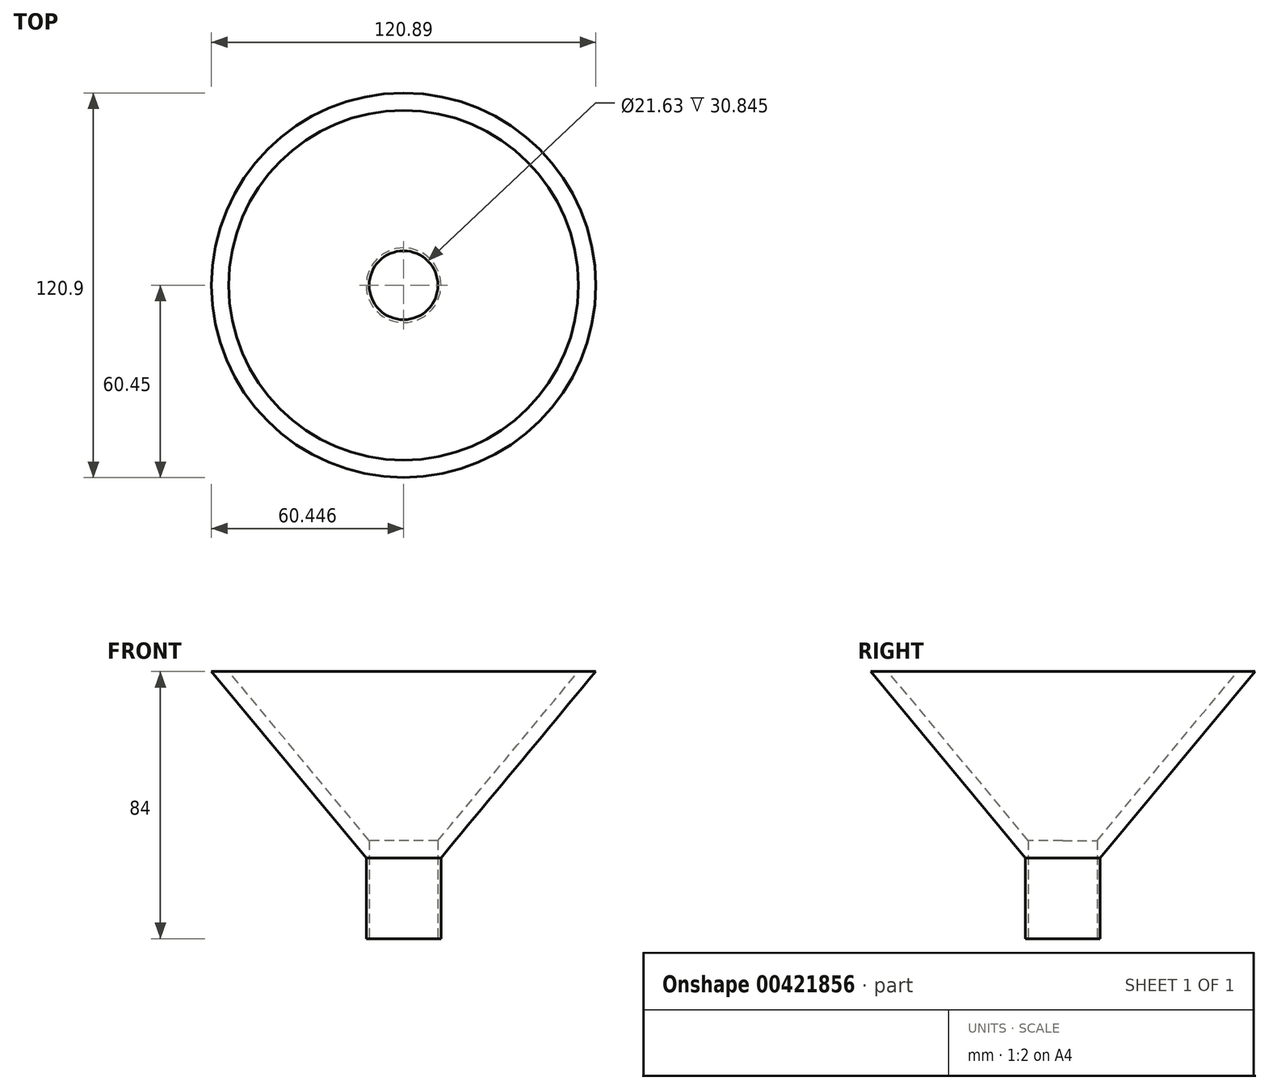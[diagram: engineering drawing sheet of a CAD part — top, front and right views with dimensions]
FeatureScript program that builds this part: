
annotation { "Feature Type Name" : "Feature", "Feature Type Description" : "" }
export const myFeature = defineFeature(function(context is Context, id is Id, definition is map)
    precondition{}
    {
        {
            var Q0;
            Q0=qCreatedBy(makeId("Front.planeOp"),FACE);
            var sketch = newSketch(context, id + "F0", { "sketchPlane" : qUnion([Q0])});
            skLineSegment(sketch, "E0", {"start": v(0, 0) * mm, "end": v(0, -25.4) * mm});
            skLineSegment(sketch, "E1", {"start": v(0, -25.4) * mm, "end": v(0, 0) * mm});
            skLineSegment(sketch, "E2", {"start": v(0, 0) * mm, "end": v(48.7, 58.6) * mm});
            skLineSegment(sketch, "E3", {"start": v(48.7, 58.6) * mm, "end": v(43.25, 58.6) * mm});
            skLineSegment(sketch, "E4", {"start": v(43.25, 58.6) * mm, "end": v(-5.45, 0) * mm});
            skLineSegment(sketch, "E5", {"start": v(-5.45, 0) * mm, "end": v(-11.74, 0) * mm});
            skLineSegment(sketch, "E6", {"start": v(-11.74, 0) * mm, "end": v(-11.74, -25.4) * mm});
            skLineSegment(sketch, "E7", {"start": v(-11.74, -25.4) * mm, "end": v(0, -25.4) * mm});
            skSolve(sketch);
        }
        {
            var Q0;
            Q0 = qSketchRegion(id + "F0", true);
            var Q1;
            Q1=sQuery(id+"F0.wireOp",EDGE,"E6");
            revolve(context, id + "F1", {"entities" : qUnion([Q0]), "axis" : qUnion([Q1]), "revolveType" : RevolveType.FULL});
        }
        {
            var Q0;
            Q0=makeQuery(id+"F1.opRevolve","SWEPT_FACE",FACE,{"disambiguationData":[OSD([sQuery(id+"F0.wireOp",EDGE,"E7")])]});
            var sketch = newSketch(context, id + "F2", { "sketchPlane" : qUnion([Q0])});
            skCircle(sketch, "E8", {"center": v(-11.74, 0) * mm, "radius": 10.82 * mm});
            skSolve(sketch);
        }
        {
            var Q0;
            Q0=makeQuery(id+"F2.imprint","IMPRINT",FACE,{"disambiguationData":[TD([[makeQuery(id+"F2.imprint","IMPRINT",EDGE,{"derivedFrom":sQuery(id+"F2.wireOp",EDGE,"E8")}),1.0]])]});
            extrude(context, id + "F3", {"entities" : qUnion([Q0]), "operationType" : NewBodyOperationType.REMOVE, "oppositeDirection" : true, "depth" : 50.8 * mm});
        }
    });
